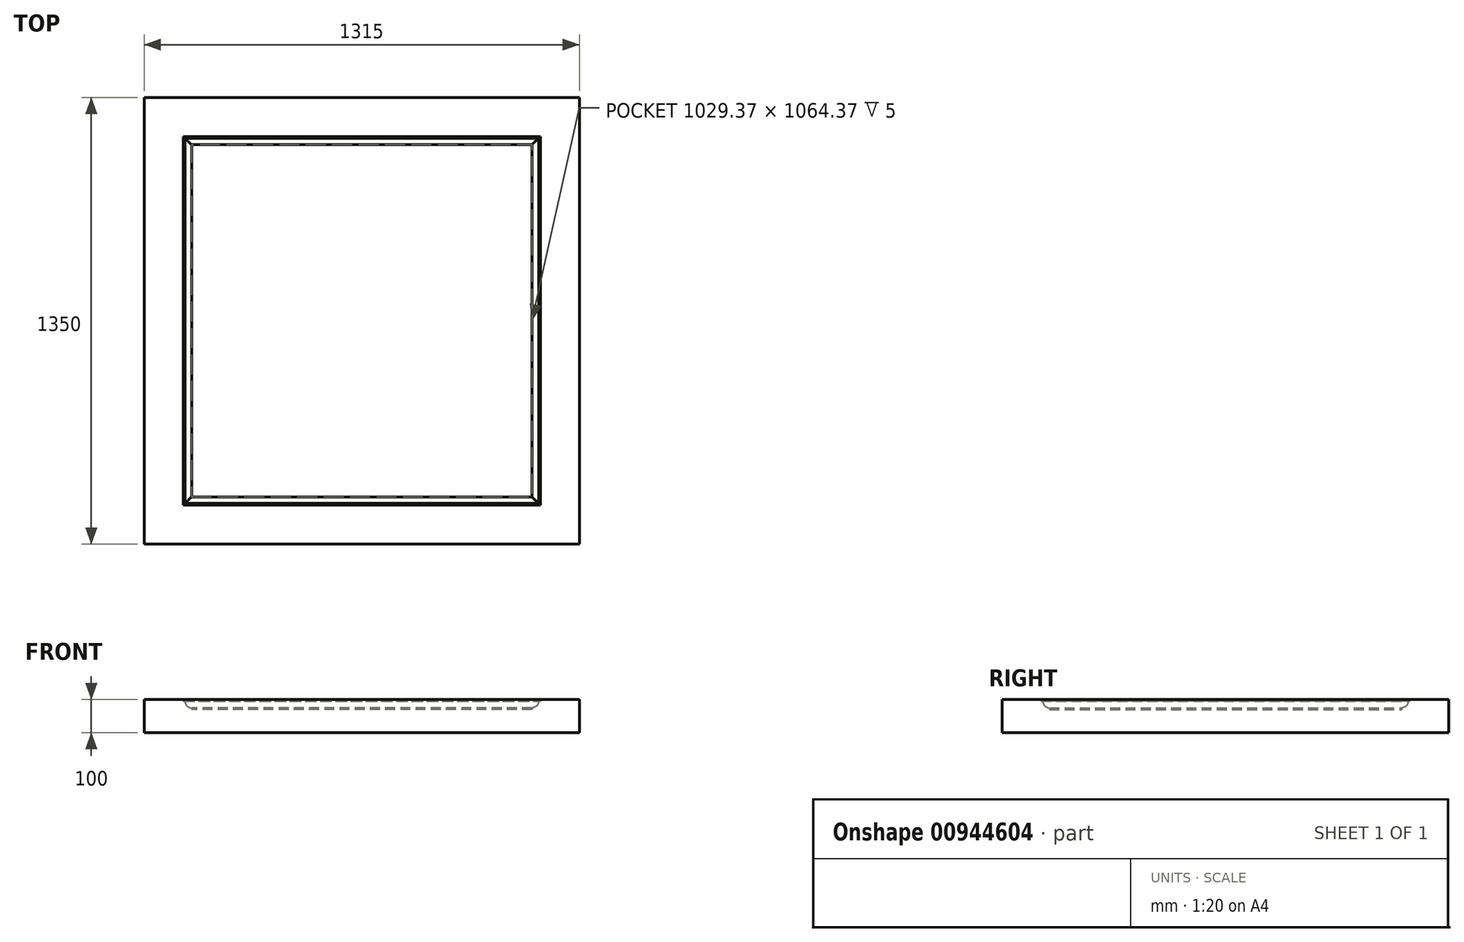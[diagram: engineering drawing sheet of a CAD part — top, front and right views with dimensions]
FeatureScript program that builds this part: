
annotation { "Feature Type Name" : "Feature", "Feature Type Description" : "" }
export const myFeature = defineFeature(function(context is Context, id is Id, definition is map)
    precondition{}
    {
        {
            var Q0;
            Q0=qCreatedBy(makeId("Top.planeOp"),FACE);
            var sketch = newSketch(context, id + "F0", { "sketchPlane" : qUnion([Q0])});
            skLineSegment(sketch, "E0.bottom", {"start": v(657.5, -675) * mm, "end": v(-657.5, -675) * mm});
            skLineSegment(sketch, "E0.top", {"start": v(657.5, 675) * mm, "end": v(-657.5, 675) * mm});
            skLineSegment(sketch, "E0.left", {"start": v(657.5, -675) * mm, "end": v(657.5, 675) * mm});
            skLineSegment(sketch, "E0.right", {"start": v(-657.5, -675) * mm, "end": v(-657.5, 675) * mm});
            skPoint(sketch, "E0.middle", {"position": v(0, 0) * mm});
            skSolve(sketch);
        }
        {
            var Q0;
            Q0=makeQuery(id+"F0.imprint","IMPRINT",FACE,{"disambiguationData":[TD([[makeQuery(id+"F0.imprint","IMPRINT",EDGE,{"derivedFrom":sQuery(id+"F0.wireOp",EDGE,"E0.bottom")}),-1.0]])]});
            extrude(context, id + "F1", {"entities" : qUnion([Q0]), "depth" : 100 * mm, "offsetDistance" : 25 * mm});
        }
        {
            var Q0;
            Q0=makeQuery(id+"F1.opExtrude","CAP_FACE",FACE,{"disambiguationData":[OSD([sQuery(id+"F0.wireOp",EDGE,"E0.bottom"),sQuery(id+"F0.wireOp",EDGE,"E0.top"),sQuery(id+"F0.wireOp",EDGE,"E0.left"),sQuery(id+"F0.wireOp",EDGE,"E0.right")])],"isStart":false});
            var sketch = newSketch(context, id + "F2", { "sketchPlane" : qUnion([Q0])});
            skLineSegment(sketch, "E1.bottom", {"start": v(550, 567.5) * mm, "end": v(-550, 567.5) * mm});
            skLineSegment(sketch, "E1.top", {"start": v(550, -567.5) * mm, "end": v(-550, -567.5) * mm});
            skLineSegment(sketch, "E1.left", {"start": v(550, 567.5) * mm, "end": v(550, -567.5) * mm});
            skLineSegment(sketch, "E1.right", {"start": v(-550, 567.5) * mm, "end": v(-550, -567.5) * mm});
            skPoint(sketch, "E1.middle", {"position": v(0, 0) * mm});
            skSolve(sketch);
        }
        {
            var Q0;
            Q0=makeQuery(id+"F2.imprint","IMPRINT",FACE,{"disambiguationData":[TD([[makeQuery(id+"F2.imprint","IMPRINT",EDGE,{"derivedFrom":sQuery(id+"F2.wireOp",EDGE,"E1.bottom")}),1.0]])]});
            extrude(context, id + "F3", {"entities" : qUnion([Q0]), "operationType" : NewBodyOperationType.REMOVE, "oppositeDirection" : true, "depth" : 30 * mm, "offsetDistance" : 25 * mm});
        }
        {
            var Q0;
            Q0=qCreatedBy(makeId("Right.planeOp"),FACE);
            var sketch = newSketch(context, id + "F4", { "sketchPlane" : qUnion([Q0])});
            skLineSegment(sketch, "E2.0", {"start": v(-567.5, 70) * mm, "end": v(-567.5, 100) * mm});
            skLineSegment(sketch, "E3", {"start": v(-567.5, 100) * mm, "end": v(-557.19, 100) * mm});
            skLineSegment(sketch, "E4", {"start": v(-557.19, 100) * mm, "end": v(-557.19, 95) * mm});
            skLineSegment(sketch, "E5", {"start": v(-557.19, 95) * mm, "end": v(-552.19, 95) * mm});
            skArc(sketch, "E6", {"start": v(-552.19, 95) * mm, "mid": v(-546.33, 80.86) * mm, "end": v(-532.19, 75) * mm});
            skLineSegment(sketch, "E7", {"start": v(-532.19, 75) * mm, "end": v(-532.19, 70) * mm});
            skLineSegment(sketch, "E8", {"start": v(-532.19, 70) * mm, "end": v(-567.5, 70) * mm});
            skSolve(sketch);
        }
        {
            var Q0;
            Q0=makeQuery(id+"F3.boolean.opBoolean","COPY",FACE,{"derivedFrom":makeQuery(id+"F3.opExtrude","CAP_FACE",FACE,{"disambiguationData":[OSD([sQuery(id+"F2.wireOp",EDGE,"E1.bottom"),sQuery(id+"F2.wireOp",EDGE,"E1.top"),sQuery(id+"F2.wireOp",EDGE,"E1.left"),sQuery(id+"F2.wireOp",EDGE,"E1.right")])],"isStart":false})});
            var sketch = newSketch(context, id + "F5", { "sketchPlane" : qUnion([Q0])});
            skLineSegment(sketch, "E9.0", {"start": v(550, 567.5) * mm, "end": v(550, -567.5) * mm});
            skLineSegment(sketch, "E9.1", {"start": v(550, -567.5) * mm, "end": v(-550, -567.5) * mm});
            skLineSegment(sketch, "E9.2", {"start": v(-550, 567.5) * mm, "end": v(-550, -567.5) * mm});
            skLineSegment(sketch, "E9.3", {"start": v(550, 567.5) * mm, "end": v(-550, 567.5) * mm});
            skSolve(sketch);
        }
        {
            var Q0;
            Q0 = qSketchRegion(id + "F4", true);
            var Q1;
            Q1 = qConstructionFilter(qBodyType(qCreatedBy(id + "F5" ,EDGE), BodyType.WIRE), ConstructionObject.NO);
            sweep(context, id + "F6", {"operationType" : NewBodyOperationType.ADD, "profiles" : qUnion([Q0]), "path" : qUnion([Q1])});
        }
    });
